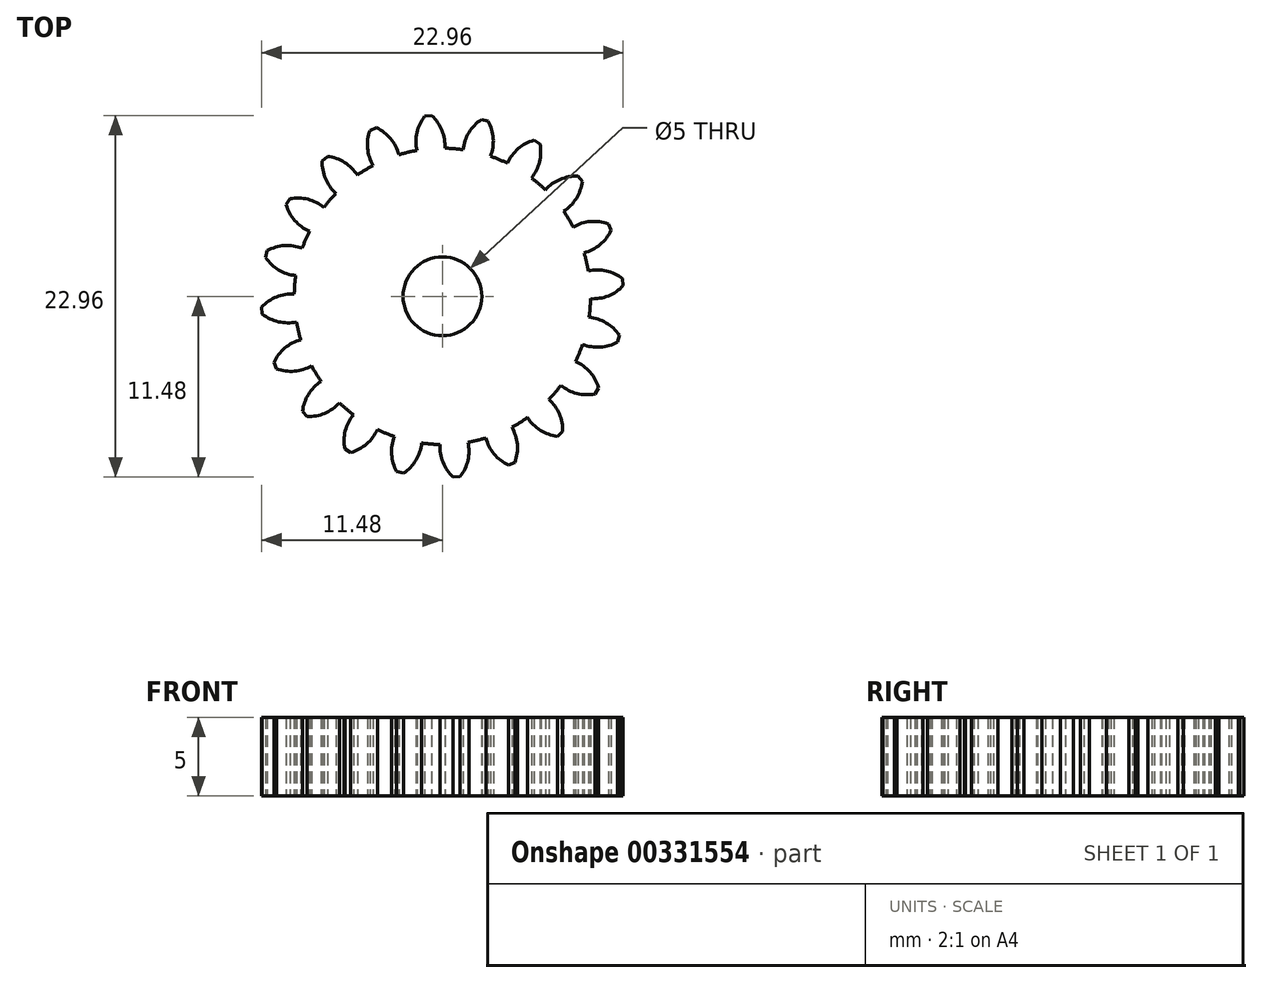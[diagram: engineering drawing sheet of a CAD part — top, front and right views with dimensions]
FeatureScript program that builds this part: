
annotation { "Feature Type Name" : "Feature", "Feature Type Description" : "" }
export const myFeature = defineFeature(function(context is Context, id is Id, definition is map)
    precondition{}
    {
        {
            assignVariable(context, id + "F0", {"name" : "GearDepth", "anyValue" : 5});
        }
        {
            var Q0;
            Q0=qCreatedBy(makeId("Top.planeOp"),FACE);
            var sketch = newSketch(context, id + "F1", { "sketchPlane" : qUnion([Q0])});
            skCircle(sketch, "E0", {"center": v(0, 0) * mm, "radius": 9.4 * mm});
            skCircle(sketch, "E1", {"center": v(0, 0) * mm, "radius": 10.45 * mm, "construction": true});
            skCircle(sketch, "E2", {"center": v(0, 0) * mm, "radius": 11.5 * mm, "construction": true});
            skLineSegment(sketch, "E3", {"start": v(0, 0) * mm, "end": v(0, 17.6) * mm, "construction": true});
            skLineSegment(sketch, "E4", {"start": v(0, 0) * mm, "end": v(-1.42, 18) * mm, "construction": true});
            skLineSegment(sketch, "E5", {"start": v(0, 10.45) * mm, "end": v(-10.54, 10.45) * mm, "construction": true});
            skLineSegment(sketch, "E6", {"start": v(0, 10.45) * mm, "end": v(-10.3, 6.7) * mm, "construction": true});
            skCircle(sketch, "E7", {"center": v(0, 10.45) * mm, "radius": 2.61 * mm, "construction": true});
            skCircle(sketch, "E8", {"center": v(-2.46, 9.56) * mm, "radius": 2.61 * mm, "construction": true});
            skArc(sketch, "E9", {"start": v(-4.91, 10.45) * mm, "mid": v(-4.92, 10.42) * mm, "end": v(-4.94, 10.39) * mm});
            skArc(sketch, "E10.trimOffspring", {"start": v(0.15, 9.4) * mm, "mid": v(-0.03, 10.54) * mm, "end": v(-0.68, 11.48) * mm});
            skArc(sketch, "E11.MirrorCS", {"start": v(-1.62, 9.27) * mm, "mid": v(-1.62, 10.41) * mm, "end": v(-1.12, 11.45) * mm});
            skLineSegment(sketch, "E12", {"start": v(-1.12, 11.45) * mm, "end": v(-0.68, 11.48) * mm});
            skArc(sketch, "E13.1.0", {"start": v(-2.76, 9) * mm, "mid": v(-3.29, 10.01) * mm, "end": v(-4.2, 10.7) * mm});
            skLineSegment(sketch, "E13.1.1", {"start": v(-4.6, 10.54) * mm, "end": v(-4.2, 10.7) * mm});
            skArc(sketch, "E13.1.2", {"start": v(-4.4, 8.31) * mm, "mid": v(-4.76, 9.4) * mm, "end": v(-4.6, 10.54) * mm});
            skArc(sketch, "E13.2.0", {"start": v(-5.4, 7.7) * mm, "mid": v(-6.22, 8.5) * mm, "end": v(-7.3, 8.89) * mm});
            skLineSegment(sketch, "E13.2.1", {"start": v(-7.64, 8.6) * mm, "end": v(-7.3, 8.89) * mm});
            skArc(sketch, "E13.2.2", {"start": v(-6.76, 6.54) * mm, "mid": v(-7.43, 7.47) * mm, "end": v(-7.64, 8.6) * mm});
            skArc(sketch, "E13.3.0", {"start": v(-7.52, 5.65) * mm, "mid": v(-8.54, 6.17) * mm, "end": v(-9.69, 6.2) * mm});
            skLineSegment(sketch, "E13.3.1", {"start": v(-9.92, 5.82) * mm, "end": v(-9.69, 6.2) * mm});
            skArc(sketch, "E13.3.2", {"start": v(-8.45, 4.13) * mm, "mid": v(-9.37, 4.81) * mm, "end": v(-9.92, 5.82) * mm});
            skArc(sketch, "E13.4.0", {"start": v(-8.9, 3.05) * mm, "mid": v(-10.03, 3.23) * mm, "end": v(-11.13, 2.9) * mm});
            skLineSegment(sketch, "E13.4.1", {"start": v(-11.23, 2.47) * mm, "end": v(-11.13, 2.9) * mm});
            skArc(sketch, "E13.4.2", {"start": v(-9.32, 1.32) * mm, "mid": v(-10.4, 1.68) * mm, "end": v(-11.23, 2.47) * mm});
            skArc(sketch, "E13.5.0", {"start": v(-9.4, 0.15) * mm, "mid": v(-10.54, -0.03) * mm, "end": v(-11.48, -0.68) * mm});
            skLineSegment(sketch, "E13.5.1", {"start": v(-11.45, -1.12) * mm, "end": v(-11.48, -0.68) * mm});
            skArc(sketch, "E13.5.2", {"start": v(-9.27, -1.62) * mm, "mid": v(-10.41, -1.62) * mm, "end": v(-11.45, -1.12) * mm});
            skArc(sketch, "E13.6.0", {"start": v(-9, -2.76) * mm, "mid": v(-10.01, -3.29) * mm, "end": v(-10.7, -4.2) * mm});
            skLineSegment(sketch, "E13.6.1", {"start": v(-10.54, -4.6) * mm, "end": v(-10.7, -4.2) * mm});
            skArc(sketch, "E13.6.2", {"start": v(-8.31, -4.4) * mm, "mid": v(-9.4, -4.76) * mm, "end": v(-10.54, -4.6) * mm});
            skArc(sketch, "E13.7.0", {"start": v(-7.7, -5.4) * mm, "mid": v(-8.5, -6.22) * mm, "end": v(-8.89, -7.3) * mm});
            skLineSegment(sketch, "E13.7.1", {"start": v(-8.6, -7.64) * mm, "end": v(-8.89, -7.3) * mm});
            skArc(sketch, "E13.7.2", {"start": v(-6.54, -6.76) * mm, "mid": v(-7.47, -7.43) * mm, "end": v(-8.6, -7.64) * mm});
            skArc(sketch, "E13.8.0", {"start": v(-5.65, -7.52) * mm, "mid": v(-6.17, -8.54) * mm, "end": v(-6.2, -9.69) * mm});
            skLineSegment(sketch, "E13.8.1", {"start": v(-5.82, -9.92) * mm, "end": v(-6.2, -9.69) * mm});
            skArc(sketch, "E13.8.2", {"start": v(-4.13, -8.45) * mm, "mid": v(-4.81, -9.37) * mm, "end": v(-5.82, -9.92) * mm});
            skArc(sketch, "E13.9.0", {"start": v(-3.05, -8.9) * mm, "mid": v(-3.23, -10.03) * mm, "end": v(-2.9, -11.13) * mm});
            skLineSegment(sketch, "E13.9.1", {"start": v(-2.47, -11.23) * mm, "end": v(-2.9, -11.13) * mm});
            skArc(sketch, "E13.9.2", {"start": v(-1.32, -9.32) * mm, "mid": v(-1.68, -10.4) * mm, "end": v(-2.47, -11.23) * mm});
            skArc(sketch, "E13.10.0", {"start": v(-0.15, -9.4) * mm, "mid": v(0.03, -10.54) * mm, "end": v(0.68, -11.48) * mm});
            skLineSegment(sketch, "E13.10.1", {"start": v(1.12, -11.45) * mm, "end": v(0.68, -11.48) * mm});
            skArc(sketch, "E13.10.2", {"start": v(1.62, -9.27) * mm, "mid": v(1.62, -10.41) * mm, "end": v(1.12, -11.45) * mm});
            skArc(sketch, "E13.11.0", {"start": v(2.76, -9) * mm, "mid": v(3.29, -10.01) * mm, "end": v(4.2, -10.7) * mm});
            skLineSegment(sketch, "E13.11.1", {"start": v(4.6, -10.54) * mm, "end": v(4.2, -10.7) * mm});
            skArc(sketch, "E13.11.2", {"start": v(4.4, -8.31) * mm, "mid": v(4.76, -9.4) * mm, "end": v(4.6, -10.54) * mm});
            skArc(sketch, "E13.12.0", {"start": v(5.4, -7.7) * mm, "mid": v(6.22, -8.5) * mm, "end": v(7.3, -8.89) * mm});
            skLineSegment(sketch, "E13.12.1", {"start": v(7.64, -8.6) * mm, "end": v(7.3, -8.89) * mm});
            skArc(sketch, "E13.12.2", {"start": v(6.76, -6.54) * mm, "mid": v(7.43, -7.47) * mm, "end": v(7.64, -8.6) * mm});
            skArc(sketch, "E13.13.0", {"start": v(7.52, -5.65) * mm, "mid": v(8.54, -6.17) * mm, "end": v(9.69, -6.2) * mm});
            skLineSegment(sketch, "E13.13.1", {"start": v(9.92, -5.82) * mm, "end": v(9.69, -6.2) * mm});
            skArc(sketch, "E13.13.2", {"start": v(8.45, -4.13) * mm, "mid": v(9.37, -4.81) * mm, "end": v(9.92, -5.82) * mm});
            skArc(sketch, "E13.14.0", {"start": v(8.9, -3.05) * mm, "mid": v(10.03, -3.23) * mm, "end": v(11.13, -2.9) * mm});
            skLineSegment(sketch, "E13.14.1", {"start": v(11.23, -2.47) * mm, "end": v(11.13, -2.9) * mm});
            skArc(sketch, "E13.14.2", {"start": v(9.32, -1.32) * mm, "mid": v(10.4, -1.68) * mm, "end": v(11.23, -2.47) * mm});
            skArc(sketch, "E13.15.0", {"start": v(9.4, -0.15) * mm, "mid": v(10.54, 0.03) * mm, "end": v(11.48, 0.68) * mm});
            skLineSegment(sketch, "E13.15.1", {"start": v(11.45, 1.12) * mm, "end": v(11.48, 0.68) * mm});
            skArc(sketch, "E13.15.2", {"start": v(9.27, 1.62) * mm, "mid": v(10.41, 1.62) * mm, "end": v(11.45, 1.12) * mm});
            skArc(sketch, "E13.16.0", {"start": v(9, 2.76) * mm, "mid": v(10.01, 3.29) * mm, "end": v(10.7, 4.2) * mm});
            skLineSegment(sketch, "E13.16.1", {"start": v(10.54, 4.6) * mm, "end": v(10.7, 4.2) * mm});
            skArc(sketch, "E13.16.2", {"start": v(8.31, 4.4) * mm, "mid": v(9.4, 4.76) * mm, "end": v(10.54, 4.6) * mm});
            skArc(sketch, "E13.17.0", {"start": v(7.7, 5.4) * mm, "mid": v(8.5, 6.22) * mm, "end": v(8.89, 7.3) * mm});
            skLineSegment(sketch, "E13.17.1", {"start": v(8.6, 7.64) * mm, "end": v(8.89, 7.3) * mm});
            skArc(sketch, "E13.17.2", {"start": v(6.54, 6.76) * mm, "mid": v(7.47, 7.43) * mm, "end": v(8.6, 7.64) * mm});
            skArc(sketch, "E13.18.0", {"start": v(5.65, 7.52) * mm, "mid": v(6.17, 8.54) * mm, "end": v(6.2, 9.69) * mm});
            skLineSegment(sketch, "E13.18.1", {"start": v(5.82, 9.92) * mm, "end": v(6.2, 9.69) * mm});
            skArc(sketch, "E13.18.2", {"start": v(4.13, 8.45) * mm, "mid": v(4.81, 9.37) * mm, "end": v(5.82, 9.92) * mm});
            skArc(sketch, "E13.19.0", {"start": v(3.05, 8.9) * mm, "mid": v(3.23, 10.03) * mm, "end": v(2.9, 11.13) * mm});
            skLineSegment(sketch, "E13.19.1", {"start": v(2.47, 11.23) * mm, "end": v(2.9, 11.13) * mm});
            skArc(sketch, "E13.19.2", {"start": v(1.32, 9.32) * mm, "mid": v(1.68, 10.4) * mm, "end": v(2.47, 11.23) * mm});
            skCircle(sketch, "E14", {"center": v(0, 0) * mm, "radius": 2.5 * mm});
            skSolve(sketch);
        }
        {
            var Q0;
            {var subQ0=sQuery(id+"F1.wireOp",EDGE,"E10.trimOffspring");Q0=makeQuery(id+"F1.imprint","IMPRINT",FACE,{"disambiguationData":[TD([[makeQuery(id+"F1.imprint","IMPRINT",EDGE,{"derivedFrom":subQ0}),1.0]])]});}
            var Q1;
            {var subQ0=sQuery(id+"F1.wireOp",EDGE,"E0");var subQ1=makeQuery(id+"F1.imprint","INTERSECT",VERTEX,{"derivedFrom":[subQ0,sQuery(id+"F1.wireOp",EDGE,"E10.trimOffspring")]});Q1=makeQuery(id+"F1.imprint","IMPRINT",FACE,{"disambiguationData":[TD([[makeQuery(id+"F1.imprint","IMPRINT",EDGE,{"disambiguationData":[TD([[subQ1,-1.0]])],"derivedFrom":subQ0}),1.0]])]});}
            var Q2;
            {var subQ0=sQuery(id+"F1.wireOp",EDGE,"E13.1.0");Q2=makeQuery(id+"F1.imprint","IMPRINT",FACE,{"disambiguationData":[TD([[makeQuery(id+"F1.imprint","IMPRINT",EDGE,{"derivedFrom":subQ0}),1.0]])]});}
            var Q3;
            {var subQ0=sQuery(id+"F1.wireOp",EDGE,"E13.2.0");Q3=makeQuery(id+"F1.imprint","IMPRINT",FACE,{"disambiguationData":[TD([[makeQuery(id+"F1.imprint","IMPRINT",EDGE,{"derivedFrom":subQ0}),1.0]])]});}
            var Q4;
            {var subQ0=sQuery(id+"F1.wireOp",EDGE,"E13.3.0");Q4=makeQuery(id+"F1.imprint","IMPRINT",FACE,{"disambiguationData":[TD([[makeQuery(id+"F1.imprint","IMPRINT",EDGE,{"derivedFrom":subQ0}),1.0]])]});}
            var Q5;
            {var subQ0=sQuery(id+"F1.wireOp",EDGE,"E13.4.0");Q5=makeQuery(id+"F1.imprint","IMPRINT",FACE,{"disambiguationData":[TD([[makeQuery(id+"F1.imprint","IMPRINT",EDGE,{"derivedFrom":subQ0}),1.0]])]});}
            var Q6;
            {var subQ0=sQuery(id+"F1.wireOp",EDGE,"E13.5.0");Q6=makeQuery(id+"F1.imprint","IMPRINT",FACE,{"disambiguationData":[TD([[makeQuery(id+"F1.imprint","IMPRINT",EDGE,{"derivedFrom":subQ0}),1.0]])]});}
            var Q7;
            {var subQ0=sQuery(id+"F1.wireOp",EDGE,"E13.6.0");Q7=makeQuery(id+"F1.imprint","IMPRINT",FACE,{"disambiguationData":[TD([[makeQuery(id+"F1.imprint","IMPRINT",EDGE,{"derivedFrom":subQ0}),1.0]])]});}
            var Q8;
            {var subQ0=sQuery(id+"F1.wireOp",EDGE,"E13.7.0");Q8=makeQuery(id+"F1.imprint","IMPRINT",FACE,{"disambiguationData":[TD([[makeQuery(id+"F1.imprint","IMPRINT",EDGE,{"derivedFrom":subQ0}),1.0]])]});}
            var Q9;
            {var subQ0=sQuery(id+"F1.wireOp",EDGE,"E13.8.0");Q9=makeQuery(id+"F1.imprint","IMPRINT",FACE,{"disambiguationData":[TD([[makeQuery(id+"F1.imprint","IMPRINT",EDGE,{"derivedFrom":subQ0}),1.0]])]});}
            var Q10;
            {var subQ0=sQuery(id+"F1.wireOp",EDGE,"E13.9.0");Q10=makeQuery(id+"F1.imprint","IMPRINT",FACE,{"disambiguationData":[TD([[makeQuery(id+"F1.imprint","IMPRINT",EDGE,{"derivedFrom":subQ0}),1.0]])]});}
            var Q11;
            {var subQ0=sQuery(id+"F1.wireOp",EDGE,"E13.10.0");Q11=makeQuery(id+"F1.imprint","IMPRINT",FACE,{"disambiguationData":[TD([[makeQuery(id+"F1.imprint","IMPRINT",EDGE,{"derivedFrom":subQ0}),1.0]])]});}
            var Q12;
            {var subQ0=sQuery(id+"F1.wireOp",EDGE,"E13.11.0");Q12=makeQuery(id+"F1.imprint","IMPRINT",FACE,{"disambiguationData":[TD([[makeQuery(id+"F1.imprint","IMPRINT",EDGE,{"derivedFrom":subQ0}),1.0]])]});}
            var Q13;
            {var subQ0=sQuery(id+"F1.wireOp",EDGE,"E13.12.0");Q13=makeQuery(id+"F1.imprint","IMPRINT",FACE,{"disambiguationData":[TD([[makeQuery(id+"F1.imprint","IMPRINT",EDGE,{"derivedFrom":subQ0}),1.0]])]});}
            var Q14;
            {var subQ0=sQuery(id+"F1.wireOp",EDGE,"E13.13.0");Q14=makeQuery(id+"F1.imprint","IMPRINT",FACE,{"disambiguationData":[TD([[makeQuery(id+"F1.imprint","IMPRINT",EDGE,{"derivedFrom":subQ0}),1.0]])]});}
            var Q15;
            {var subQ0=sQuery(id+"F1.wireOp",EDGE,"E13.14.0");Q15=makeQuery(id+"F1.imprint","IMPRINT",FACE,{"disambiguationData":[TD([[makeQuery(id+"F1.imprint","IMPRINT",EDGE,{"derivedFrom":subQ0}),1.0]])]});}
            var Q16;
            {var subQ0=sQuery(id+"F1.wireOp",EDGE,"E13.15.0");Q16=makeQuery(id+"F1.imprint","IMPRINT",FACE,{"disambiguationData":[TD([[makeQuery(id+"F1.imprint","IMPRINT",EDGE,{"derivedFrom":subQ0}),1.0]])]});}
            var Q17;
            {var subQ0=sQuery(id+"F1.wireOp",EDGE,"E13.16.0");Q17=makeQuery(id+"F1.imprint","IMPRINT",FACE,{"disambiguationData":[TD([[makeQuery(id+"F1.imprint","IMPRINT",EDGE,{"derivedFrom":subQ0}),1.0]])]});}
            var Q18;
            {var subQ0=sQuery(id+"F1.wireOp",EDGE,"E13.17.0");Q18=makeQuery(id+"F1.imprint","IMPRINT",FACE,{"disambiguationData":[TD([[makeQuery(id+"F1.imprint","IMPRINT",EDGE,{"derivedFrom":subQ0}),1.0]])]});}
            var Q19;
            {var subQ0=sQuery(id+"F1.wireOp",EDGE,"E13.18.0");Q19=makeQuery(id+"F1.imprint","IMPRINT",FACE,{"disambiguationData":[TD([[makeQuery(id+"F1.imprint","IMPRINT",EDGE,{"derivedFrom":subQ0}),1.0]])]});}
            var Q20;
            {var subQ0=sQuery(id+"F1.wireOp",EDGE,"E13.19.0");Q20=makeQuery(id+"F1.imprint","IMPRINT",FACE,{"disambiguationData":[TD([[makeQuery(id+"F1.imprint","IMPRINT",EDGE,{"derivedFrom":subQ0}),1.0]])]});}
            var Q21;
            Q21=sQuery(id+"F1.wireOp",EDGE,"E0");
            var Q22;
            Q22=sQuery(id+"F1.wireOp",EDGE,"E10.trimOffspring");
            var Q23;
            Q23=sQuery(id+"F1.wireOp",EDGE,"E12");
            var Q24;
            Q24=sQuery(id+"F1.wireOp",EDGE,"E11.MirrorCS");
            extrude(context, id + "F2", {"entities" : qUnion([Q0, Q1, Q2, Q3, Q4, Q5, Q6, Q7, Q8, Q9, Q10, Q11, Q12, Q13, Q14, Q15, Q16, Q17, Q18, Q19, Q20]), "surfaceEntities" : qUnion([Q21, Q22, Q23, Q24]), "depth" : (getVariable(context, 'GearDepth')) * mm});
        }
    });
